# Revit family: НЕВАТОМ_Решетка РВ-1_20220407
name_source: partatom
category: Воздухораспределители
revit_build: Autodesk Revit 2017 (Build: 20170118_1100(x64)
units: mm (PartAtom-declared; Revit-internal decimal feet)

## family parameters
Всегда вертикально = Да
На основе рабочей плоскости = Нет
Общий = Нет
При загрузке вырезать с полостями = Нет
Размер круглого соединителя = Использовать диаметр
Тип детали = Нормальный
Точка расчета площади = Нет

## types (24) — shared parameters
ADSK_Единица измерения = шт.
ADSK_Завод-изготовитель = NEVATOM
ADSK_Материал наименование = Алюминий
ADSK_Наименование = Решетка вентиляционная внутренняя
H = 35 мм
H/4 = 9 мм
Nevatom_URL = https://t.me
Ключевая пометка = Вентиляция
Материал = Полиацеталь, белый
zero-valued in all types: ADSK_Масса, ADSK_Размер_Высота, ADSK_Размер_Длина, ADSK_Размер_Ширина

## per-type parameters (varying)
| type | -B/2 | A | A+25 | A-25 | B | B+25 | B-25 | B/2 | n | ΔPmax | ΔPmin | Макс. расход | Макс. расход воздуха | Мин. расход | Минимальный расход воздуха |
| РВ-1-100х150 | -63 мм | 100 мм | 125 мм | 75 мм | 150 мм | 175 мм | 125 мм | 63 мм | 2 | 58.4 Па | 0.9 Па | 250.0 м³/ч | 250.0 м³/ч | 30.0 м³/ч | 30.0 м³/ч |
| РВ-1-500х500 | -238 мм | 500 мм | 525 мм | 475 мм | 500 мм | 525 мм | 475 мм | 238 мм | 10 | 6.1 Па | 0.3 Па | 1900.0 м³/ч | 1900.0 м³/ч | 400.0 м³/ч | 400.0 м³/ч |
| РВ-1-100х200 | -88 мм | 100 мм | 125 мм | 75 мм | 200 мм | 225 мм | 175 мм | 88 мм | 2 | 43.5 Па | 0.4 Па | 300.0 м³/ч | 300.0 м³/ч | 30.0 м³/ч | 30.0 м³/ч |
| РВ-1-100х250 | -113 мм | 100 мм | 125 мм | 75 мм | 250 мм | 275 мм | 225 мм | 113 мм | 2 | 29.4 Па | 0.5 Па | 320.0 м³/ч | 320.0 м³/ч | 40.0 м³/ч | 40.0 м³/ч |
| РВ-1-100х300 | -138 мм | 100 мм | 125 мм | 75 мм | 300 мм | 325 мм | 275 мм | 138 мм | 2 | 22.6 Па | 0.4 Па | 350.0 м³/ч | 350.0 м³/ч | 50.0 м³/ч | 50.0 м³/ч |
| РВ-1-100х400 | -188 мм | 100 мм | 125 мм | 75 мм | 400 мм | 425 мм | 375 мм | 188 мм | 2 | 17.5 Па | 0.4 Па | 400.0 м³/ч | 400.0 м³/ч | 65.0 м³/ч | 65.0 м³/ч |
| РВ-1-100х500 | -238 мм | 100 мм | 125 мм | 75 мм | 500 мм | 525 мм | 475 мм | 238 мм | 2 | 16.4 Па | 0.4 Па | 520.0 м³/ч | 520.0 м³/ч | 80.0 м³/ч | 80.0 м³/ч |
| РВ-1-150х150 | -63 мм | 150 мм | 175 мм | 125 мм | 150 мм | 175 мм | 125 мм | 63 мм | 3 | 29.5 Па | 0.4 Па | 350.0 м³/ч | 350.0 м³/ч | 35.0 м³/ч | 35.0 м³/ч |
| РВ-1-150х200 | -88 мм | 150 мм | 175 мм | 125 мм | 200 мм | 225 мм | 175 мм | 88 мм | 3 | 22.7 Па | 0.4 Па | 350.0 м³/ч | 350.0 м³/ч | 50.0 м³/ч | 50.0 м³/ч |
| РВ-1-150х250 | -113 мм | 150 мм | 175 мм | 125 мм | 250 мм | 275 мм | 225 мм | 113 мм | 3 | 17.4 Па | 0.5 Па | 400.0 м³/ч | 400.0 м³/ч | 70.0 м³/ч | 70.0 м³/ч |
| РВ-1-150х300 | -138 мм | 150 мм | 175 мм | 125 мм | 300 мм | 325 мм | 275 мм | 138 мм | 3 | 20.7 Па | 0.5 Па | 520.0 м³/ч | 520.0 м³/ч | 80.0 м³/ч | 80.0 м³/ч |
| РВ-1-150х400 | -188 мм | 150 мм | 175 мм | 125 мм | 400 мм | 425 мм | 375 мм | 188 мм | 3 | 13.2 Па | 0.4 Па | 600.0 м³/ч | 600.0 м³/ч | 100.0 м³/ч | 100.0 м³/ч |
| РВ-1-150х500 | -238 мм | 150 мм | 175 мм | 125 мм | 500 мм | 525 мм | 475 мм | 238 мм | 3 | 16.4 Па | 0.4 Па | 800.0 м³/ч | 800.0 м³/ч | 130.0 м³/ч | 130.0 м³/ч |
| РВ-1-200х200 | -88 мм | 200 мм | 225 мм | 175 мм | 200 мм | 225 мм | 175 мм | 88 мм | 4 | 16.4 Па | 0.5 Па | 400.0 м³/ч | 400.0 м³/ч | 70.0 м³/ч | 70.0 м³/ч |
| РВ-1-200х250 | -113 мм | 200 мм | 225 мм | 175 мм | 250 мм | 275 мм | 225 мм | 113 мм | 4 | 16.3 Па | 0.4 Па | 500.0 м³/ч | 500.0 м³/ч | 80.0 м³/ч | 80.0 м³/ч |
| РВ-1-200х300 | -138 мм | 200 мм | 225 мм | 175 мм | 300 мм | 325 мм | 275 мм | 138 мм | 4 | 14.6 Па | 0.4 Па | 600.0 м³/ч | 600.0 м³/ч | 100.0 м³/ч | 100.0 м³/ч |
| РВ-1-200х400 | -188 мм | 200 мм | 225 мм | 175 мм | 400 мм | 425 мм | 375 мм | 188 мм | 4 | 13.4 Па | 0.4 Па | 800.0 м³/ч | 800.0 м³/ч | 130.0 м³/ч | 130.0 м³/ч |
| РВ-1-200х500 | -238 мм | 200 мм | 225 мм | 175 мм | 500 мм | 525 мм | 475 мм | 238 мм | 4 | 11.9 Па | 0.4 Па | 1000.0 м³/ч | 1000.0 м³/ч | 160.0 м³/ч | 160.0 м³/ч |
| РВ-1-300х300 | -138 мм | 300 мм | 325 мм | 275 мм | 300 мм | 325 мм | 275 мм | 138 мм | 6 | 13.6 Па | 0.4 Па | 900.0 м³/ч | 900.0 м³/ч | 150.0 м³/ч | 150.0 м³/ч |
| РВ-1-300х400 | -188 мм | 300 мм | 325 мм | 275 мм | 400 мм | 425 мм | 375 мм | 188 мм | 6 | 13.4 Па | 0.4 Па | 1200.0 м³/ч | 1200.0 м³/ч | 200.0 м³/ч | 200.0 м³/ч |
| РВ-1-300х500 | -238 мм | 300 мм | 325 мм | 275 мм | 500 мм | 525 мм | 475 мм | 238 мм | 6 | 12.6 Па | 0.4 Па | 1450.0 м³/ч | 1450.0 м³/ч | 250.0 м³/ч | 250.0 м³/ч |
| РВ-1-300х600 | -288 мм | 300 мм | 325 мм | 275 мм | 600 мм | 625 мм | 575 мм | 288 мм | 6 | 10.4 Па | 0.4 Па | 1500.0 м³/ч | 1500.0 м³/ч | 300.0 м³/ч | 300.0 м³/ч |
| РВ-1-400х400 | -188 мм | 400 мм | 425 мм | 375 мм | 400 мм | 425 мм | 375 мм | 188 мм | 8 | 10.5 Па | 0.4 Па | 1450.0 м³/ч | 1450.0 м³/ч | 250.0 м³/ч | 250.0 м³/ч |
| РВ-1-400х500 | -238 мм | 400 мм | 425 мм | 375 мм | 500 мм | 525 мм | 475 мм | 238 мм | 8 | 8.2 Па | 0.4 Па | 1500.0 м³/ч | 1500.0 м³/ч | 300.0 м³/ч | 300.0 м³/ч |

note: column(s) folded — value = type name in every type: ADSK_Марка
